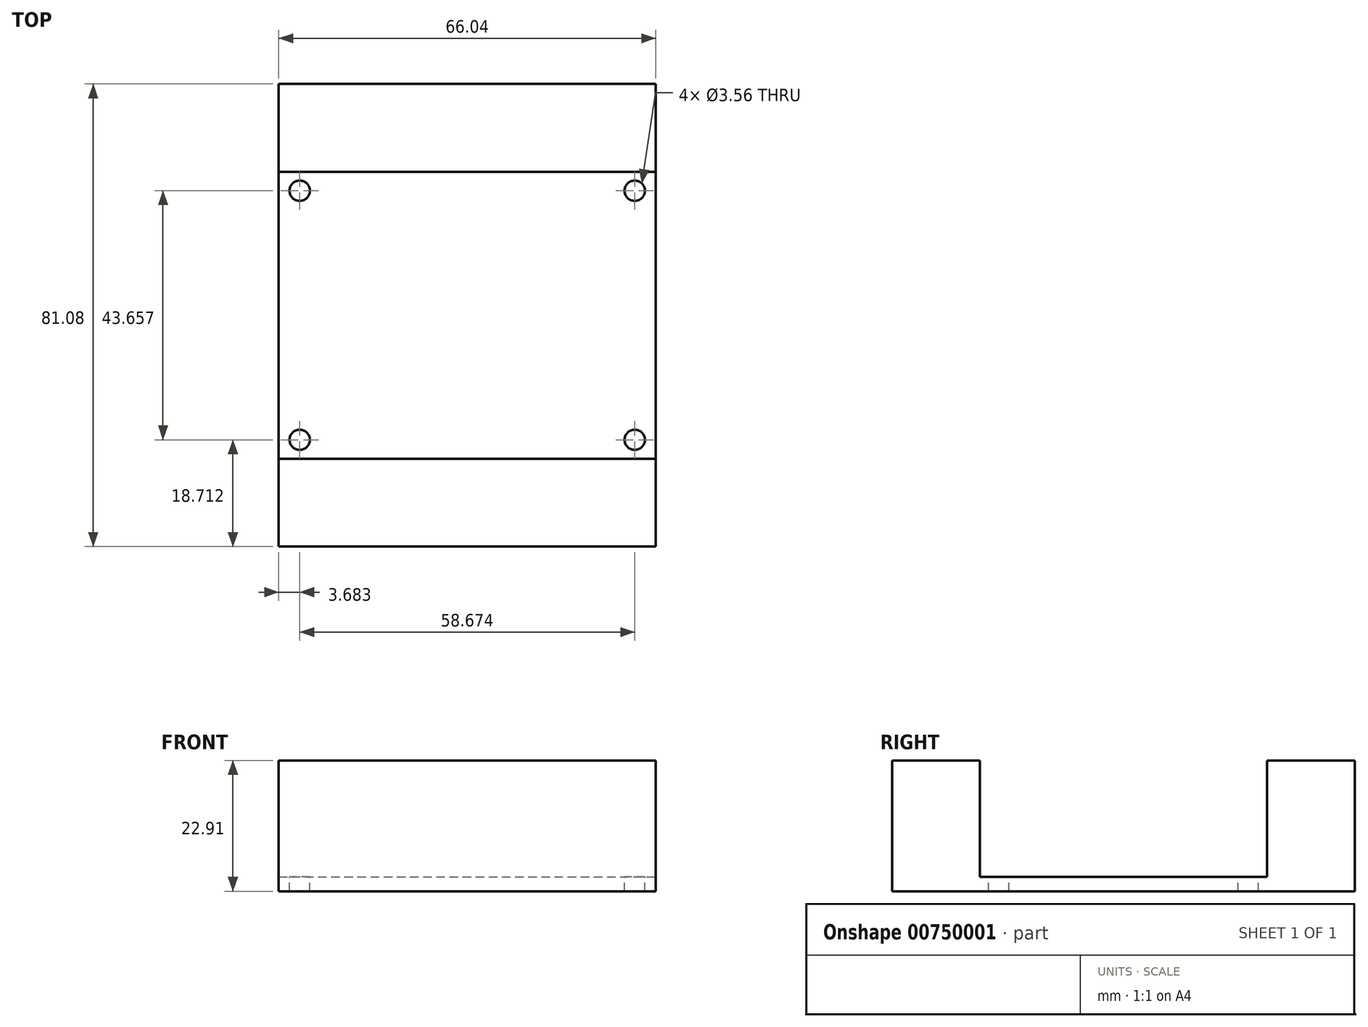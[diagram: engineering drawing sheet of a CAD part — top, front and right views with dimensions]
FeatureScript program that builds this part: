
annotation { "Feature Type Name" : "Feature", "Feature Type Description" : "" }
export const myFeature = defineFeature(function(context is Context, id is Id, definition is map)
    precondition{}
    {
        {
            var Q0;
            Q0=qCreatedBy(makeId("Top.planeOp"),FACE);
            var sketch = newSketch(context, id + "F0", { "sketchPlane" : qUnion([Q0])});
            skLineSegment(sketch, "E0.bottom", {"start": v(33.02, -40.54) * mm, "end": v(-33.02, -40.54) * mm});
            skLineSegment(sketch, "E0.top", {"start": v(33.02, 40.54) * mm, "end": v(-33.02, 40.54) * mm});
            skLineSegment(sketch, "E0.left", {"start": v(33.02, -40.54) * mm, "end": v(33.02, 40.54) * mm});
            skLineSegment(sketch, "E0.right", {"start": v(-33.02, -40.54) * mm, "end": v(-33.02, 40.54) * mm});
            skPoint(sketch, "E0.middle", {"position": v(0, 0) * mm});
            skSolve(sketch);
        }
        {
            var Q0;
            Q0 = qSketchRegion(id + "F0", true);
            extrude(context, id + "F1", {"entities" : qUnion([Q0]), "depth" : 2.54 * mm, "offsetDistance" : 25 * mm});
        }
        {
            var Q0;
            Q0=makeQuery(id+"F1.opExtrude","CAP_FACE",FACE,{"disambiguationData":[OSD([sQuery(id+"F0.wireOp",EDGE,"E0.bottom"),sQuery(id+"F0.wireOp",EDGE,"E0.top"),sQuery(id+"F0.wireOp",EDGE,"E0.left"),sQuery(id+"F0.wireOp",EDGE,"E0.right")])],"isStart":false});
            var sketch = newSketch(context, id + "F2", { "sketchPlane" : qUnion([Q0])});
            skLineSegment(sketch, "E1.bottom", {"start": v(-33.02, 40.54) * mm, "end": v(33.02, 40.54) * mm});
            skLineSegment(sketch, "E1.top", {"start": v(-33.02, 25.16) * mm, "end": v(33.02, 25.16) * mm});
            skLineSegment(sketch, "E1.left", {"start": v(-33.02, 40.54) * mm, "end": v(-33.02, 25.16) * mm});
            skLineSegment(sketch, "E1.right", {"start": v(33.02, 40.54) * mm, "end": v(33.02, 25.16) * mm});
            skLineSegment(sketch, "E2.MirrorCS", {"start": v(-33.02, -25.16) * mm, "end": v(33.02, -25.16) * mm});
            skLineSegment(sketch, "E3.MirrorCS", {"start": v(-33.02, -40.54) * mm, "end": v(33.02, -40.54) * mm});
            skLineSegment(sketch, "E4.MirrorCS", {"start": v(33.02, -40.54) * mm, "end": v(33.02, -25.16) * mm});
            skLineSegment(sketch, "E5.MirrorCS", {"start": v(-33.02, -40.54) * mm, "end": v(-33.02, -25.16) * mm});
            skSolve(sketch);
        }
        {
            var Q0;
            Q0 = qSketchRegion(id + "F2", true);
            extrude(context, id + "F3", {"entities" : qUnion([Q0]), "operationType" : NewBodyOperationType.ADD, "depth" : 20.37 * mm, "offsetDistance" : 25 * mm});
        }
        {
            var Q0;
            Q0=makeQuery(id+"F1.opExtrude","CAP_FACE",FACE,{"disambiguationData":[OSD([sQuery(id+"F0.wireOp",EDGE,"E0.bottom"),sQuery(id+"F0.wireOp",EDGE,"E0.top"),sQuery(id+"F0.wireOp",EDGE,"E0.left"),sQuery(id+"F0.wireOp",EDGE,"E0.right")])],"isStart":false});
            var sketch = newSketch(context, id + "F4", { "sketchPlane" : qUnion([Q0])});
            skCircle(sketch, "E6", {"center": v(-29.34, 21.83) * mm, "radius": 1.78 * mm});
            skCircle(sketch, "E7.MirrorC", {"center": v(29.34, 21.83) * mm, "radius": 1.78 * mm});
            skCircle(sketch, "E8.MirrorC", {"center": v(29.34, -21.83) * mm, "radius": 1.78 * mm});
            skCircle(sketch, "E9.MirrorC", {"center": v(-29.34, -21.83) * mm, "radius": 1.78 * mm});
            skSolve(sketch);
        }
        {
            var Q0;
            Q0 = qSketchRegion(id + "F4", true);
            extrude(context, id + "F5", {"entities" : qUnion([Q0]), "operationType" : NewBodyOperationType.REMOVE, "oppositeDirection" : true, "depth" : 25 * mm, "offsetDistance" : 25 * mm});
        }
    });
